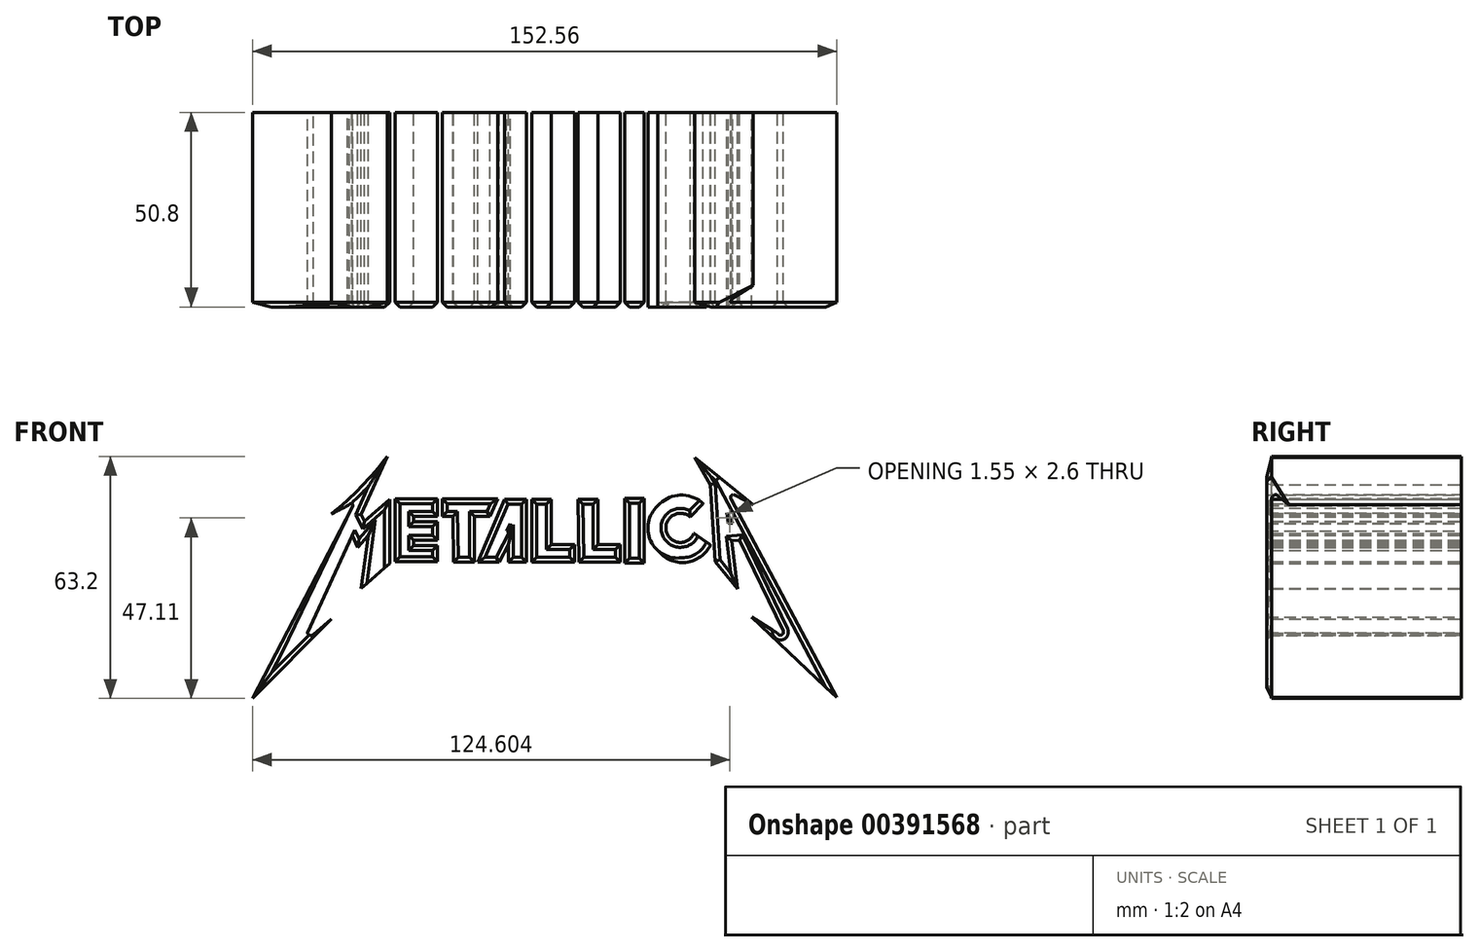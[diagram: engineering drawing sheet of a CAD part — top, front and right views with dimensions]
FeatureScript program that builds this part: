
annotation { "Feature Type Name" : "Feature", "Feature Type Description" : "" }
export const myFeature = defineFeature(function(context is Context, id is Id, definition is map)
    precondition{}
    {
        {
            var Q0;
            Q0=qCreatedBy(makeId("Front.planeOp"),FACE);
            var sketch = newSketch(context, id + "F0", { "sketchPlane" : qUnion([Q0])});
            skLineSegment(sketch, "E0", {"start": v(-27.93, 36.84) * mm, "end": v(-27.93, 32.23) * mm});
            skLineSegment(sketch, "E1", {"start": v(-27.93, 36.84) * mm, "end": v(-39.04, 36.84) * mm});
            skLineSegment(sketch, "E2", {"start": v(-39.04, 36.84) * mm, "end": v(-39.04, 20.51) * mm});
            skLineSegment(sketch, "E3", {"start": v(-39.04, 20.51) * mm, "end": v(-27.93, 20.51) * mm});
            skLineSegment(sketch, "E4", {"start": v(-27.93, 20.51) * mm, "end": v(-27.93, 24.64) * mm});
            skLineSegment(sketch, "E5", {"start": v(-27.93, 24.64) * mm, "end": v(-34.16, 24.64) * mm});
            skLineSegment(sketch, "E6", {"start": v(-34.16, 24.64) * mm, "end": v(-34.16, 26.07) * mm});
            skLineSegment(sketch, "E7", {"start": v(-34.16, 26.07) * mm, "end": v(-27.93, 26.07) * mm});
            skLineSegment(sketch, "E8", {"start": v(-27.93, 26.07) * mm, "end": v(-27.93, 30.88) * mm});
            skLineSegment(sketch, "E9", {"start": v(-27.93, 30.88) * mm, "end": v(-34.16, 30.88) * mm});
            skLineSegment(sketch, "E10", {"start": v(-34.16, 30.88) * mm, "end": v(-34.16, 32.23) * mm});
            skLineSegment(sketch, "E11", {"start": v(-27.93, 32.23) * mm, "end": v(-34.16, 32.23) * mm});
            skLineSegment(sketch, "E12", {"start": v(-23.73, 20.38) * mm, "end": v(-18.24, 20.38) * mm});
            skLineSegment(sketch, "E13", {"start": v(-18.24, 20.38) * mm, "end": v(-18.24, 32.23) * mm});
            skLineSegment(sketch, "E14", {"start": v(-18.24, 32.23) * mm, "end": v(-14.17, 32.23) * mm});
            skLineSegment(sketch, "E15", {"start": v(-14.17, 32.23) * mm, "end": v(-12.2, 36.84) * mm});
            skLineSegment(sketch, "E16", {"start": v(-12.2, 36.84) * mm, "end": v(-26.64, 36.84) * mm});
            skLineSegment(sketch, "E17", {"start": v(-26.64, 36.84) * mm, "end": v(-26.64, 32.23) * mm});
            skLineSegment(sketch, "E18", {"start": v(-26.64, 32.23) * mm, "end": v(-23.93, 32.23) * mm});
            skLineSegment(sketch, "E19", {"start": v(-23.93, 32.23) * mm, "end": v(-23.73, 20.38) * mm});
            skLineSegment(sketch, "E20", {"start": v(-10.35, 36.77) * mm, "end": v(-4.7, 36.77) * mm});
            skLineSegment(sketch, "E21", {"start": v(-4.7, 36.77) * mm, "end": v(-4.7, 20.3) * mm});
            skLineSegment(sketch, "E22", {"start": v(-4.7, 20.3) * mm, "end": v(-9.45, 20.3) * mm});
            skLineSegment(sketch, "E23", {"start": v(-9.45, 20.3) * mm, "end": v(-9.45, 24.89) * mm});
            skLineSegment(sketch, "E24", {"start": v(-9.45, 24.89) * mm, "end": v(-11.81, 20.3) * mm});
            skLineSegment(sketch, "E25", {"start": v(-11.81, 20.3) * mm, "end": v(-17.43, 20.3) * mm});
            skLineSegment(sketch, "E26", {"start": v(-17.43, 20.3) * mm, "end": v(-10.35, 36.77) * mm});
            skLineSegment(sketch, "E27", {"start": v(-8.94, 30.38) * mm, "end": v(-8.94, 28.5) * mm});
            skLineSegment(sketch, "E28", {"start": v(-8.94, 28.5) * mm, "end": v(-9.92, 28.5) * mm});
            skLineSegment(sketch, "E29", {"start": v(-9.92, 28.5) * mm, "end": v(-8.94, 30.38) * mm});
            skLineSegment(sketch, "E30", {"start": v(-3.28, 36.77) * mm, "end": v(1.83, 36.77) * mm});
            skLineSegment(sketch, "E31", {"start": v(1.83, 36.77) * mm, "end": v(1.83, 24.89) * mm});
            skLineSegment(sketch, "E32", {"start": v(1.83, 24.89) * mm, "end": v(7.92, 24.89) * mm});
            skLineSegment(sketch, "E33", {"start": v(7.92, 24.89) * mm, "end": v(7.92, 20.3) * mm});
            skLineSegment(sketch, "E34", {"start": v(7.92, 20.3) * mm, "end": v(-3.28, 20.3) * mm});
            skLineSegment(sketch, "E35", {"start": v(-3.28, 20.3) * mm, "end": v(-3.28, 36.77) * mm});
            skLineSegment(sketch, "E36", {"start": v(8.78, 36.77) * mm, "end": v(13.94, 36.77) * mm});
            skLineSegment(sketch, "E37", {"start": v(13.94, 36.77) * mm, "end": v(13.94, 24.89) * mm});
            skLineSegment(sketch, "E38", {"start": v(13.94, 24.89) * mm, "end": v(19.76, 24.89) * mm});
            skLineSegment(sketch, "E39", {"start": v(19.76, 24.89) * mm, "end": v(19.76, 20.3) * mm});
            skLineSegment(sketch, "E40", {"start": v(19.76, 20.3) * mm, "end": v(9, 20.3) * mm});
            skLineSegment(sketch, "E41", {"start": v(9, 20.3) * mm, "end": v(8.78, 36.77) * mm});
            skLineSegment(sketch, "E42.bottom", {"start": v(20.99, 36.97) * mm, "end": v(26.06, 36.97) * mm});
            skLineSegment(sketch, "E42.top", {"start": v(20.99, 20.13) * mm, "end": v(26.06, 20.13) * mm});
            skLineSegment(sketch, "E42.left", {"start": v(20.99, 36.97) * mm, "end": v(20.99, 20.13) * mm});
            skLineSegment(sketch, "E42.right", {"start": v(26.06, 36.97) * mm, "end": v(26.06, 20.13) * mm});
            skArc(sketch, "E43", {"start": v(38.07, 32.1) * mm, "mid": v(31.8, 28.43) * mm, "end": v(39.04, 27.83) * mm});
            skLineSegment(sketch, "E44", {"start": v(38.07, 32.1) * mm, "end": v(41.46, 35.62) * mm});
            skLineSegment(sketch, "E45", {"start": v(39.04, 27.83) * mm, "end": v(43.39, 24.81) * mm});
            skArc(sketch, "E46", {"start": v(41.46, 35.62) * mm, "mid": v(35.4, 37.8) * mm, "end": v(29.6, 35) * mm});
            skArc(sketch, "E47", {"start": v(29.6, 35) * mm, "mid": v(27, 29.19) * mm, "end": v(29.6, 23.37) * mm});
            skArc(sketch, "E48", {"start": v(29.6, 23.37) * mm, "mid": v(36.9, 20.26) * mm, "end": v(43.39, 24.81) * mm});
            skLineSegment(sketch, "E49", {"start": v(-48.72, 24.1) * mm, "end": v(-46, 27.26) * mm});
            skLineSegment(sketch, "E50", {"start": v(-46, 27.26) * mm, "end": v(-47.82, 13.52) * mm});
            skLineSegment(sketch, "E51", {"start": v(-47.82, 13.52) * mm, "end": v(-40.44, 19.99) * mm});
            skLineSegment(sketch, "E52", {"start": v(-40.44, 19.99) * mm, "end": v(-40.44, 36.7) * mm});
            skLineSegment(sketch, "E53", {"start": v(-40.44, 36.7) * mm, "end": v(-47, 31) * mm});
            skLineSegment(sketch, "E54", {"start": v(-47, 31) * mm, "end": v(-47.86, 32.72) * mm});
            skLineSegment(sketch, "E55", {"start": v(-47.86, 32.72) * mm, "end": v(-41.07, 47.94) * mm});
            skLineSegment(sketch, "E56", {"start": v(-48.72, 24.1) * mm, "end": v(-50.2, 27.26) * mm});
            skLineSegment(sketch, "E57", {"start": v(-50.2, 27.26) * mm, "end": v(-61.84, 1.86) * mm});
            skLineSegment(sketch, "E58", {"start": v(-50.35, 34.46) * mm, "end": v(-76.2, -15.26) * mm});
            skLineSegment(sketch, "E59", {"start": v(-76.2, -15.26) * mm, "end": v(-55.57, 5.47) * mm});
            skArc(sketch, "E60", {"start": v(-61.84, 1.86) * mm, "mid": v(-61.24, 1.24) * mm, "end": v(-60.38, 1.4) * mm});
            skLineSegment(sketch, "E61", {"start": v(-60.38, 1.4) * mm, "end": v(-55.57, 5.47) * mm});
            skArc(sketch, "E62", {"start": v(-55.59, 32.9) * mm, "mid": v(-47.85, 39.96) * mm, "end": v(-41.07, 47.94) * mm});
            skLineSegment(sketch, "E63", {"start": v(-55.59, 32.9) * mm, "end": v(-51.46, 35.01) * mm});
            skArc(sketch, "E64", {"start": v(-50.08, 35.01) * mm, "mid": v(-50.3, 35.57) * mm, "end": v(-50.87, 35.41) * mm});
            skLineSegment(sketch, "E65", {"start": v(-50.87, 35.41) * mm, "end": v(-51.46, 35.01) * mm});
            skLineSegment(sketch, "E66", {"start": v(-50.08, 35.01) * mm, "end": v(-50.35, 34.46) * mm});
            skLineSegment(sketch, "E67", {"start": v(44.56, 20.46) * mm, "end": v(50.43, 13.31) * mm});
            skLineSegment(sketch, "E68", {"start": v(50.43, 13.31) * mm, "end": v(48.92, 25.91) * mm});
            skLineSegment(sketch, "E69", {"start": v(48.92, 25.91) * mm, "end": v(50.96, 26.06) * mm});
            skLineSegment(sketch, "E70", {"start": v(50.96, 26.06) * mm, "end": v(62.33, 2.4) * mm});
            skLineSegment(sketch, "E71", {"start": v(44.56, 20.46) * mm, "end": v(43.3, 40.5) * mm});
            skLineSegment(sketch, "E72", {"start": v(43.3, 40.5) * mm, "end": v(39.22, 47.7) * mm});
            skLineSegment(sketch, "E73", {"start": v(39.22, 47.7) * mm, "end": v(54.52, 35.35) * mm});
            skLineSegment(sketch, "E74", {"start": v(54.52, 35.35) * mm, "end": v(49.67, 37.85) * mm});
            skLineSegment(sketch, "E75", {"start": v(48.76, 36.75) * mm, "end": v(76.35, -15.02) * mm});
            skArc(sketch, "E76", {"start": v(60.89, 1.75) * mm, "mid": v(61.94, 1.33) * mm, "end": v(62.33, 2.4) * mm});
            skLineSegment(sketch, "E77", {"start": v(60.89, 1.75) * mm, "end": v(54.15, 6.04) * mm});
            skLineSegment(sketch, "E78", {"start": v(54.15, 6.04) * mm, "end": v(76.35, -15.02) * mm});
            skArc(sketch, "E79", {"start": v(49.67, 37.85) * mm, "mid": v(48.77, 37.66) * mm, "end": v(48.76, 36.75) * mm});
            skLineSegment(sketch, "E80", {"start": v(47.62, 33.15) * mm, "end": v(49.17, 30.55) * mm});
            skLineSegment(sketch, "E81", {"start": v(49.17, 30.55) * mm, "end": v(48.02, 30.55) * mm});
            skLineSegment(sketch, "E82", {"start": v(48.02, 30.55) * mm, "end": v(47.62, 33.15) * mm});
            skSolve(sketch);
        }
        {
            var Q0;
            Q0=makeQuery(id+"F0.imprint","IMPRINT",FACE,{"disambiguationData":[TD([[makeQuery(id+"F0.imprint","IMPRINT",EDGE,{"derivedFrom":sQuery(id+"F0.wireOp",EDGE,"E49")}),1.0]])]});
            var Q1;
            Q1=makeQuery(id+"F0.imprint","IMPRINT",FACE,{"disambiguationData":[TD([[makeQuery(id+"F0.imprint","IMPRINT",EDGE,{"derivedFrom":sQuery(id+"F0.wireOp",EDGE,"E0")}),-1.0]])]});
            var Q2;
            Q2=makeQuery(id+"F0.imprint","IMPRINT",FACE,{"disambiguationData":[TD([[makeQuery(id+"F0.imprint","IMPRINT",EDGE,{"derivedFrom":sQuery(id+"F0.wireOp",EDGE,"E12")}),1.0]])]});
            var Q3;
            Q3=makeQuery(id+"F0.imprint","IMPRINT",FACE,{"disambiguationData":[TD([[makeQuery(id+"F0.imprint","IMPRINT",EDGE,{"derivedFrom":sQuery(id+"F0.wireOp",EDGE,"E20")}),-1.0]])]});
            var Q4;
            Q4=makeQuery(id+"F0.imprint","IMPRINT",FACE,{"disambiguationData":[TD([[makeQuery(id+"F0.imprint","IMPRINT",EDGE,{"derivedFrom":sQuery(id+"F0.wireOp",EDGE,"E30")}),-1.0]])]});
            var Q5;
            Q5=makeQuery(id+"F0.imprint","IMPRINT",FACE,{"disambiguationData":[TD([[makeQuery(id+"F0.imprint","IMPRINT",EDGE,{"derivedFrom":sQuery(id+"F0.wireOp",EDGE,"E36")}),-1.0]])]});
            var Q6;
            Q6=makeQuery(id+"F0.imprint","IMPRINT",FACE,{"disambiguationData":[TD([[makeQuery(id+"F0.imprint","IMPRINT",EDGE,{"derivedFrom":sQuery(id+"F0.wireOp",EDGE,"E42.bottom")}),-1.0]])]});
            var Q7;
            Q7=makeQuery(id+"F0.imprint","IMPRINT",FACE,{"disambiguationData":[TD([[makeQuery(id+"F0.imprint","IMPRINT",EDGE,{"derivedFrom":sQuery(id+"F0.wireOp",EDGE,"E43")}),-1.0]])]});
            var Q8;
            Q8=makeQuery(id+"F0.imprint","IMPRINT",FACE,{"disambiguationData":[TD([[makeQuery(id+"F0.imprint","IMPRINT",EDGE,{"derivedFrom":sQuery(id+"F0.wireOp",EDGE,"E67")}),1.0]])]});
            extrude(context, id + "F1", {"entities" : qUnion([Q0, Q1, Q2, Q3, Q4, Q5, Q6, Q7, Q8]), "depth" : 50.8 * mm});
        }
        {
            var Q0;
            Q0=makeQuery(id+"F1.opExtrude","CAP_EDGE",EDGE,{"disambiguationData":[OSD([sQuery(id+"F0.wireOp",EDGE,"E73")])],"isStart":false});
            var Q1;
            Q1=makeQuery(id+"F1.opExtrude","CAP_EDGE",EDGE,{"disambiguationData":[OSD([sQuery(id+"F0.wireOp",EDGE,"E72")])],"isStart":false});
            var Q2;
            Q2=makeQuery(id+"F1.opExtrude","CAP_EDGE",EDGE,{"disambiguationData":[OSD([sQuery(id+"F0.wireOp",EDGE,"E71")])],"isStart":false});
            var Q3;
            Q3=makeQuery(id+"F1.opExtrude","CAP_EDGE",EDGE,{"disambiguationData":[OSD([sQuery(id+"F0.wireOp",EDGE,"E75")])],"isStart":false});
            var Q4;
            Q4=makeQuery(id+"F1.opExtrude","CAP_EDGE",EDGE,{"disambiguationData":[OSD([sQuery(id+"F0.wireOp",EDGE,"E69")])],"isStart":false});
            var Q5;
            Q5=makeQuery(id+"F1.opExtrude","CAP_EDGE",EDGE,{"disambiguationData":[OSD([sQuery(id+"F0.wireOp",EDGE,"E68")])],"isStart":false});
            var Q6;
            Q6=makeQuery(id+"F1.opExtrude","CAP_EDGE",EDGE,{"disambiguationData":[OSD([sQuery(id+"F0.wireOp",EDGE,"E67")])],"isStart":false});
            var Q7;
            Q7=makeQuery(id+"F1.opExtrude","CAP_EDGE",EDGE,{"disambiguationData":[OSD([sQuery(id+"F0.wireOp",EDGE,"E70")])],"isStart":false});
            var Q8;
            Q8=makeQuery(id+"F1.opExtrude","CAP_EDGE",EDGE,{"disambiguationData":[OSD([sQuery(id+"F0.wireOp",EDGE,"E48")])],"isStart":false});
            var Q9;
            Q9=makeQuery(id+"F1.opExtrude","CAP_EDGE",EDGE,{"disambiguationData":[OSD([sQuery(id+"F0.wireOp",EDGE,"E43")])],"isStart":false});
            var Q10;
            Q10=makeQuery(id+"F1.opExtrude","CAP_EDGE",EDGE,{"disambiguationData":[OSD([sQuery(id+"F0.wireOp",EDGE,"E44")])],"isStart":false});
            var Q11;
            Q11=makeQuery(id+"F1.opExtrude","CAP_EDGE",EDGE,{"disambiguationData":[OSD([sQuery(id+"F0.wireOp",EDGE,"E42.bottom")])],"isStart":false});
            var Q12;
            Q12=makeQuery(id+"F1.opExtrude","CAP_EDGE",EDGE,{"disambiguationData":[OSD([sQuery(id+"F0.wireOp",EDGE,"E42.right")])],"isStart":false});
            var Q13;
            Q13=makeQuery(id+"F1.opExtrude","CAP_EDGE",EDGE,{"disambiguationData":[OSD([sQuery(id+"F0.wireOp",EDGE,"E42.left")])],"isStart":false});
            var Q14;
            Q14=makeQuery(id+"F1.opExtrude","CAP_EDGE",EDGE,{"disambiguationData":[OSD([sQuery(id+"F0.wireOp",EDGE,"E42.top")])],"isStart":false});
            var Q15;
            Q15=makeQuery(id+"F1.opExtrude","CAP_EDGE",EDGE,{"disambiguationData":[OSD([sQuery(id+"F0.wireOp",EDGE,"E37")])],"isStart":false});
            var Q16;
            Q16=makeQuery(id+"F1.opExtrude","CAP_EDGE",EDGE,{"disambiguationData":[OSD([sQuery(id+"F0.wireOp",EDGE,"E36")])],"isStart":false});
            var Q17;
            Q17=makeQuery(id+"F1.opExtrude","CAP_FACE",FACE,{"disambiguationData":[OSD([sQuery(id+"F0.wireOp",EDGE,"E36"),sQuery(id+"F0.wireOp",EDGE,"E37"),sQuery(id+"F0.wireOp",EDGE,"E38"),sQuery(id+"F0.wireOp",EDGE,"E39"),sQuery(id+"F0.wireOp",EDGE,"E40"),sQuery(id+"F0.wireOp",EDGE,"E41")])],"isStart":false});
            var Q18;
            Q18=makeQuery(id+"F1.opExtrude","CAP_EDGE",EDGE,{"disambiguationData":[OSD([sQuery(id+"F0.wireOp",EDGE,"E30")])],"isStart":false});
            var Q19;
            Q19=makeQuery(id+"F1.opExtrude","CAP_EDGE",EDGE,{"disambiguationData":[OSD([sQuery(id+"F0.wireOp",EDGE,"E35")])],"isStart":false});
            var Q20;
            Q20=makeQuery(id+"F1.opExtrude","CAP_EDGE",EDGE,{"disambiguationData":[OSD([sQuery(id+"F0.wireOp",EDGE,"E31")])],"isStart":false});
            var Q21;
            Q21=makeQuery(id+"F1.opExtrude","CAP_FACE",FACE,{"disambiguationData":[OSD([sQuery(id+"F0.wireOp",EDGE,"E30"),sQuery(id+"F0.wireOp",EDGE,"E31"),sQuery(id+"F0.wireOp",EDGE,"E32"),sQuery(id+"F0.wireOp",EDGE,"E33"),sQuery(id+"F0.wireOp",EDGE,"E34"),sQuery(id+"F0.wireOp",EDGE,"E35")])],"isStart":false});
            var Q22;
            Q22=makeQuery(id+"F1.opExtrude","CAP_EDGE",EDGE,{"disambiguationData":[OSD([sQuery(id+"F0.wireOp",EDGE,"E21")])],"isStart":false});
            var Q23;
            Q23=makeQuery(id+"F1.opExtrude","CAP_EDGE",EDGE,{"disambiguationData":[OSD([sQuery(id+"F0.wireOp",EDGE,"E20")])],"isStart":false});
            var Q24;
            Q24=makeQuery(id+"F1.opExtrude","CAP_EDGE",EDGE,{"disambiguationData":[OSD([sQuery(id+"F0.wireOp",EDGE,"E26")])],"isStart":false});
            var Q25;
            Q25=makeQuery(id+"F1.opExtrude","CAP_EDGE",EDGE,{"disambiguationData":[OSD([sQuery(id+"F0.wireOp",EDGE,"E25")])],"isStart":false});
            var Q26;
            Q26=makeQuery(id+"F1.opExtrude","CAP_EDGE",EDGE,{"disambiguationData":[OSD([sQuery(id+"F0.wireOp",EDGE,"E22")])],"isStart":false});
            var Q27;
            Q27=makeQuery(id+"F1.opExtrude","CAP_EDGE",EDGE,{"disambiguationData":[OSD([sQuery(id+"F0.wireOp",EDGE,"E23")])],"isStart":false});
            var Q28;
            Q28=makeQuery(id+"F1.opExtrude","CAP_EDGE",EDGE,{"disambiguationData":[OSD([sQuery(id+"F0.wireOp",EDGE,"E24")])],"isStart":false});
            var Q29;
            Q29=makeQuery(id+"F1.opExtrude","CAP_EDGE",EDGE,{"disambiguationData":[OSD([sQuery(id+"F0.wireOp",EDGE,"E15")])],"isStart":false});
            var Q30;
            Q30=makeQuery(id+"F1.opExtrude","CAP_EDGE",EDGE,{"disambiguationData":[OSD([sQuery(id+"F0.wireOp",EDGE,"E16")])],"isStart":false});
            var Q31;
            Q31=makeQuery(id+"F1.opExtrude","CAP_EDGE",EDGE,{"disambiguationData":[OSD([sQuery(id+"F0.wireOp",EDGE,"E17")])],"isStart":false});
            var Q32;
            Q32=makeQuery(id+"F1.opExtrude","CAP_EDGE",EDGE,{"disambiguationData":[OSD([sQuery(id+"F0.wireOp",EDGE,"E18")])],"isStart":false});
            var Q33;
            Q33=makeQuery(id+"F1.opExtrude","CAP_EDGE",EDGE,{"disambiguationData":[OSD([sQuery(id+"F0.wireOp",EDGE,"E14")])],"isStart":false});
            var Q34;
            Q34=makeQuery(id+"F1.opExtrude","CAP_EDGE",EDGE,{"disambiguationData":[OSD([sQuery(id+"F0.wireOp",EDGE,"E12")])],"isStart":false});
            var Q35;
            Q35=makeQuery(id+"F1.opExtrude","CAP_EDGE",EDGE,{"disambiguationData":[OSD([sQuery(id+"F0.wireOp",EDGE,"E19")])],"isStart":false});
            var Q36;
            Q36=makeQuery(id+"F1.opExtrude","CAP_EDGE",EDGE,{"disambiguationData":[OSD([sQuery(id+"F0.wireOp",EDGE,"E13")])],"isStart":false});
            var Q37;
            Q37=makeQuery(id+"F1.opExtrude","CAP_EDGE",EDGE,{"disambiguationData":[OSD([sQuery(id+"F0.wireOp",EDGE,"E1")])],"isStart":false});
            var Q38;
            Q38=makeQuery(id+"F1.opExtrude","CAP_EDGE",EDGE,{"disambiguationData":[OSD([sQuery(id+"F0.wireOp",EDGE,"E2")])],"isStart":false});
            var Q39;
            Q39=makeQuery(id+"F1.opExtrude","CAP_EDGE",EDGE,{"disambiguationData":[OSD([sQuery(id+"F0.wireOp",EDGE,"E11")])],"isStart":false});
            var Q40;
            Q40=makeQuery(id+"F1.opExtrude","CAP_EDGE",EDGE,{"disambiguationData":[OSD([sQuery(id+"F0.wireOp",EDGE,"E0")])],"isStart":false});
            var Q41;
            Q41=makeQuery(id+"F1.opExtrude","CAP_EDGE",EDGE,{"disambiguationData":[OSD([sQuery(id+"F0.wireOp",EDGE,"E9")])],"isStart":false});
            var Q42;
            Q42=makeQuery(id+"F1.opExtrude","CAP_EDGE",EDGE,{"disambiguationData":[OSD([sQuery(id+"F0.wireOp",EDGE,"E3")])],"isStart":false});
            var Q43;
            Q43=makeQuery(id+"F1.opExtrude","CAP_EDGE",EDGE,{"disambiguationData":[OSD([sQuery(id+"F0.wireOp",EDGE,"E4")])],"isStart":false});
            var Q44;
            Q44=makeQuery(id+"F1.opExtrude","CAP_FACE",FACE,{"disambiguationData":[OSD([sQuery(id+"F0.wireOp",EDGE,"E0"),sQuery(id+"F0.wireOp",EDGE,"E1"),sQuery(id+"F0.wireOp",EDGE,"E2"),sQuery(id+"F0.wireOp",EDGE,"E3"),sQuery(id+"F0.wireOp",EDGE,"E4"),sQuery(id+"F0.wireOp",EDGE,"E5"),sQuery(id+"F0.wireOp",EDGE,"E6"),sQuery(id+"F0.wireOp",EDGE,"E7"),sQuery(id+"F0.wireOp",EDGE,"E8"),sQuery(id+"F0.wireOp",EDGE,"E9"),sQuery(id+"F0.wireOp",EDGE,"E10"),sQuery(id+"F0.wireOp",EDGE,"E11")])],"isStart":false});
            var Q45;
            Q45=makeQuery(id+"F1.opExtrude","CAP_EDGE",EDGE,{"disambiguationData":[OSD([sQuery(id+"F0.wireOp",EDGE,"E55")])],"isStart":false});
            var Q46;
            Q46=makeQuery(id+"F1.opExtrude","CAP_EDGE",EDGE,{"disambiguationData":[OSD([sQuery(id+"F0.wireOp",EDGE,"E49")])],"isStart":false});
            var Q47;
            Q47=makeQuery(id+"F1.opExtrude","CAP_EDGE",EDGE,{"disambiguationData":[OSD([sQuery(id+"F0.wireOp",EDGE,"E56")])],"isStart":false});
            var Q48;
            Q48=makeQuery(id+"F1.opExtrude","CAP_EDGE",EDGE,{"disambiguationData":[OSD([sQuery(id+"F0.wireOp",EDGE,"E50")])],"isStart":false});
            var Q49;
            Q49=makeQuery(id+"F1.opExtrude","CAP_EDGE",EDGE,{"disambiguationData":[OSD([sQuery(id+"F0.wireOp",EDGE,"E52")])],"isStart":false});
            var Q50;
            Q50=makeQuery(id+"F1.opExtrude","CAP_EDGE",EDGE,{"disambiguationData":[OSD([sQuery(id+"F0.wireOp",EDGE,"E53")])],"isStart":false});
            var Q51;
            Q51=makeQuery(id+"F1.opExtrude","CAP_EDGE",EDGE,{"disambiguationData":[OSD([sQuery(id+"F0.wireOp",EDGE,"E54")])],"isStart":false});
            var Q52;
            Q52=makeQuery(id+"F1.opExtrude","CAP_EDGE",EDGE,{"disambiguationData":[OSD([sQuery(id+"F0.wireOp",EDGE,"E62")])],"isStart":false});
            var Q53;
            Q53=makeQuery(id+"F1.opExtrude","CAP_EDGE",EDGE,{"disambiguationData":[OSD([sQuery(id+"F0.wireOp",EDGE,"E58")])],"isStart":false});
            var Q54;
            Q54=makeQuery(id+"F1.opExtrude","CAP_EDGE",EDGE,{"disambiguationData":[OSD([sQuery(id+"F0.wireOp",EDGE,"E59")])],"isStart":false});
            chamfer(context, id + "F2", {"entities" : qUnion([Q0, Q1, Q2, Q3, Q4, Q5, Q6, Q7, Q8, Q9, Q10, Q11, Q12, Q13, Q14, Q15, Q16, Q17, Q18, Q19, Q20, Q21, Q22, Q23, Q24, Q25, Q26, Q27, Q28, Q29, Q30, Q31, Q32, Q33, Q34, Q35, Q36, Q37, Q38, Q39, Q40, Q41, Q42, Q43, Q44, Q45, Q46, Q47, Q48, Q49, Q50, Q51, Q52, Q53, Q54]), "width" : 1.27 * mm, "tangentPropagation" : true});
        }
    });
